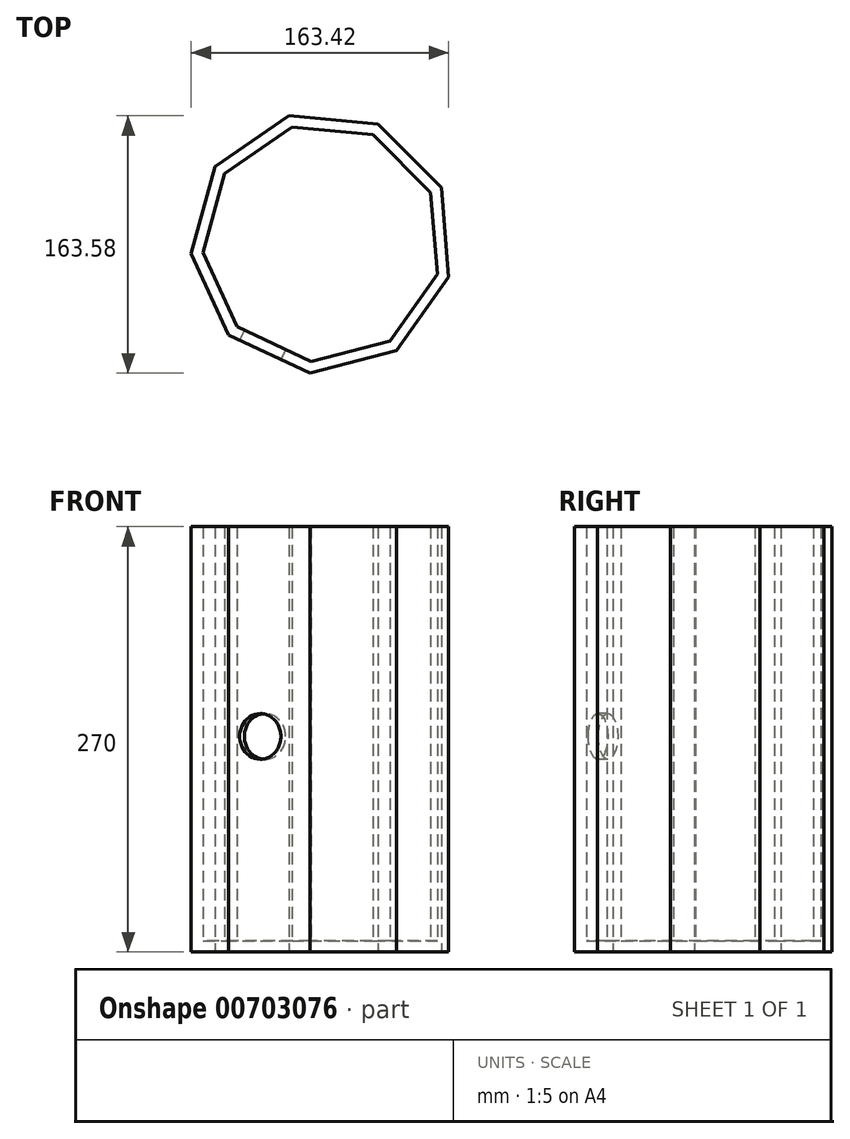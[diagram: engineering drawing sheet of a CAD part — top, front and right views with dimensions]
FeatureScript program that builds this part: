
annotation { "Feature Type Name" : "Feature", "Feature Type Description" : "" }
export const myFeature = defineFeature(function(context is Context, id is Id, definition is map)
    precondition{}
    {
        {
            var Q0;
            Q0=qCreatedBy(makeId("Top.planeOp"),FACE);
            var sketch = newSketch(context, id + "F0", { "sketchPlane" : qUnion([Q0])});
            skCircle(sketch, "E0.cCircle", {"center": v(0, 0) * mm, "radius": 78.3 * mm, "construction": true});
            skLineSegment(sketch, "E0.0", {"start": v(80.37, -22.01) * mm, "end": v(47.42, -68.52) * mm});
            skLineSegment(sketch, "E0.1", {"start": v(47.42, -68.52) * mm, "end": v(-7.72, -82.97) * mm});
            skLineSegment(sketch, "E0.2", {"start": v(-7.72, -82.97) * mm, "end": v(-59.25, -58.6) * mm});
            skLineSegment(sketch, "E0.3", {"start": v(-59.25, -58.6) * mm, "end": v(-83.05, -6.8) * mm});
            skLineSegment(sketch, "E0.4", {"start": v(-83.05, -6.8) * mm, "end": v(-68, 48.17) * mm});
            skLineSegment(sketch, "E0.5", {"start": v(-68, 48.17) * mm, "end": v(-21.12, 80.6) * mm});
            skLineSegment(sketch, "E0.6", {"start": v(-21.12, 80.6) * mm, "end": v(35.63, 75.32) * mm});
            skLineSegment(sketch, "E0.7", {"start": v(35.63, 75.32) * mm, "end": v(75.72, 34.8) * mm});
            skLineSegment(sketch, "E0.8", {"start": v(75.72, 34.8) * mm, "end": v(80.37, -22.01) * mm});
            skPoint(sketch, "E0.0.midPoint", {"position": v(63.9, -45.27) * mm});
            skSolve(sketch);
        }
        {
            var Q0;
            Q0 = qSketchRegion(id + "F0", true);
            extrude(context, id + "F1", {"entities" : qUnion([Q0]), "depth" : 270 * mm, "offsetDistance" : 25 * mm});
        }
        {
            var Q0;
            Q0=makeQuery(id+"F1.opExtrude","CAP_FACE",FACE,{"disambiguationData":[OSD([sQuery(id+"F0.wireOp",EDGE,"E0.0"),sQuery(id+"F0.wireOp",EDGE,"E0.1"),sQuery(id+"F0.wireOp",EDGE,"E0.2"),sQuery(id+"F0.wireOp",EDGE,"E0.3"),sQuery(id+"F0.wireOp",EDGE,"E0.4"),sQuery(id+"F0.wireOp",EDGE,"E0.5"),sQuery(id+"F0.wireOp",EDGE,"E0.6"),sQuery(id+"F0.wireOp",EDGE,"E0.7"),sQuery(id+"F0.wireOp",EDGE,"E0.8")])],"isStart":false});
            shell(context, id + "F2", {"entities" : qUnion([Q0]), "thickness" : 7 * mm});
        }
        {
            var Q0;
            Q0=makeQuery(id+"F1.opExtrude","SWEPT_FACE",FACE,{"disambiguationData":[OSD([sQuery(id+"F0.wireOp",EDGE,"E0.2")])]});
            var sketch = newSketch(context, id + "F3", { "sketchPlane" : qUnion([Q0])});
            skCircle(sketch, "E1", {"center": v(-6.37, 136.8) * mm, "radius": 14.52 * mm});
            skSolve(sketch);
        }
        {
            var Q0;
            Q0 = qSketchRegion(id + "F3", true);
            extrude(context, id + "F4", {"entities" : qUnion([Q0]), "operationType" : NewBodyOperationType.REMOVE, "oppositeDirection" : true, "depth" : 25 * mm, "offsetDistance" : 25 * mm});
        }
    });
